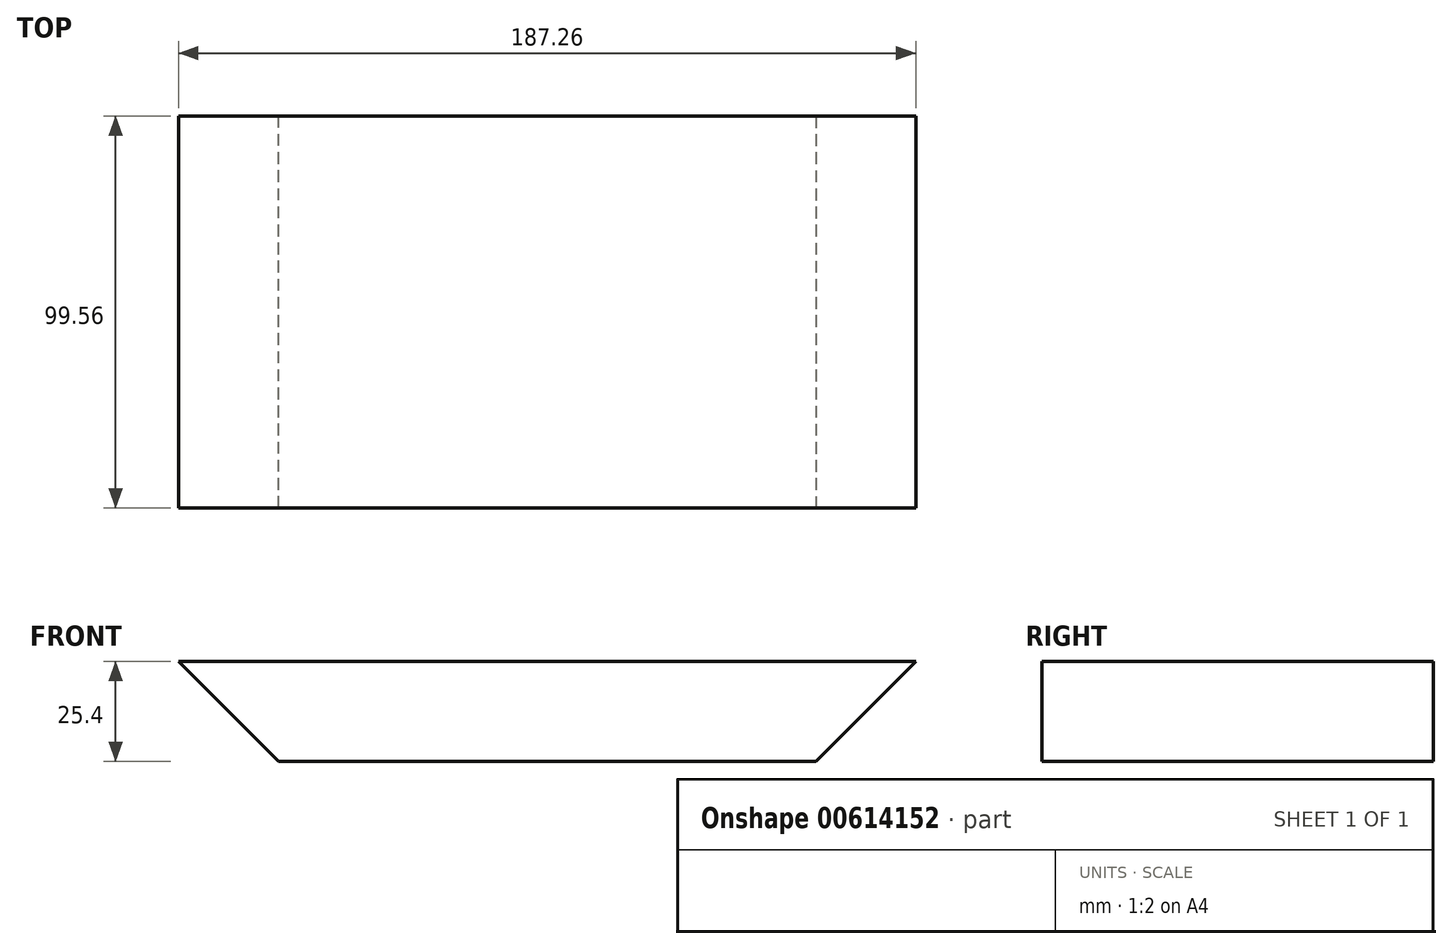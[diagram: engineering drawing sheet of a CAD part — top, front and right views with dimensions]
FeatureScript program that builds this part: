
annotation { "Feature Type Name" : "Feature", "Feature Type Description" : "" }
export const myFeature = defineFeature(function(context is Context, id is Id, definition is map)
    precondition{}
    {
        {
            var Q0;
            Q0=qCreatedBy(makeId("Top.planeOp"),FACE);
            var sketch = newSketch(context, id + "F0", { "sketchPlane" : qUnion([Q0])});
            skLineSegment(sketch, "E0.bottom", {"start": v(-93.63, -49.78) * mm, "end": v(93.63, -49.78) * mm});
            skLineSegment(sketch, "E0.top", {"start": v(-93.63, 49.78) * mm, "end": v(93.63, 49.78) * mm});
            skLineSegment(sketch, "E0.left", {"start": v(-93.63, -49.78) * mm, "end": v(-93.63, 49.78) * mm});
            skLineSegment(sketch, "E0.right", {"start": v(93.63, -49.78) * mm, "end": v(93.63, 49.78) * mm});
            skPoint(sketch, "E0.middle", {"position": v(0, 0) * mm});
            skSolve(sketch);
        }
        {
            var Q0;
            Q0 = qSketchRegion(id + "F0", true);
            extrude(context, id + "F1", {"entities" : qUnion([Q0]), "depth" : 25.4 * mm, "offsetDistance" : 25.4 * mm});
        }
        {
            var Q0;
            Q0=makeQuery(id+"F1.opExtrude","CAP_EDGE",EDGE,{"disambiguationData":[OSD([sQuery(id+"F0.wireOp",EDGE,"E0.left")])],"isStart":true});
            var Q1;
            Q1=makeQuery(id+"F1.opExtrude","CAP_EDGE",EDGE,{"disambiguationData":[OSD([sQuery(id+"F0.wireOp",EDGE,"E0.right")])],"isStart":true});
            chamfer(context, id + "F2", {"entities" : qUnion([Q0, Q1]), "width" : 25.4 * mm, "tangentPropagation" : true});
        }
    });
